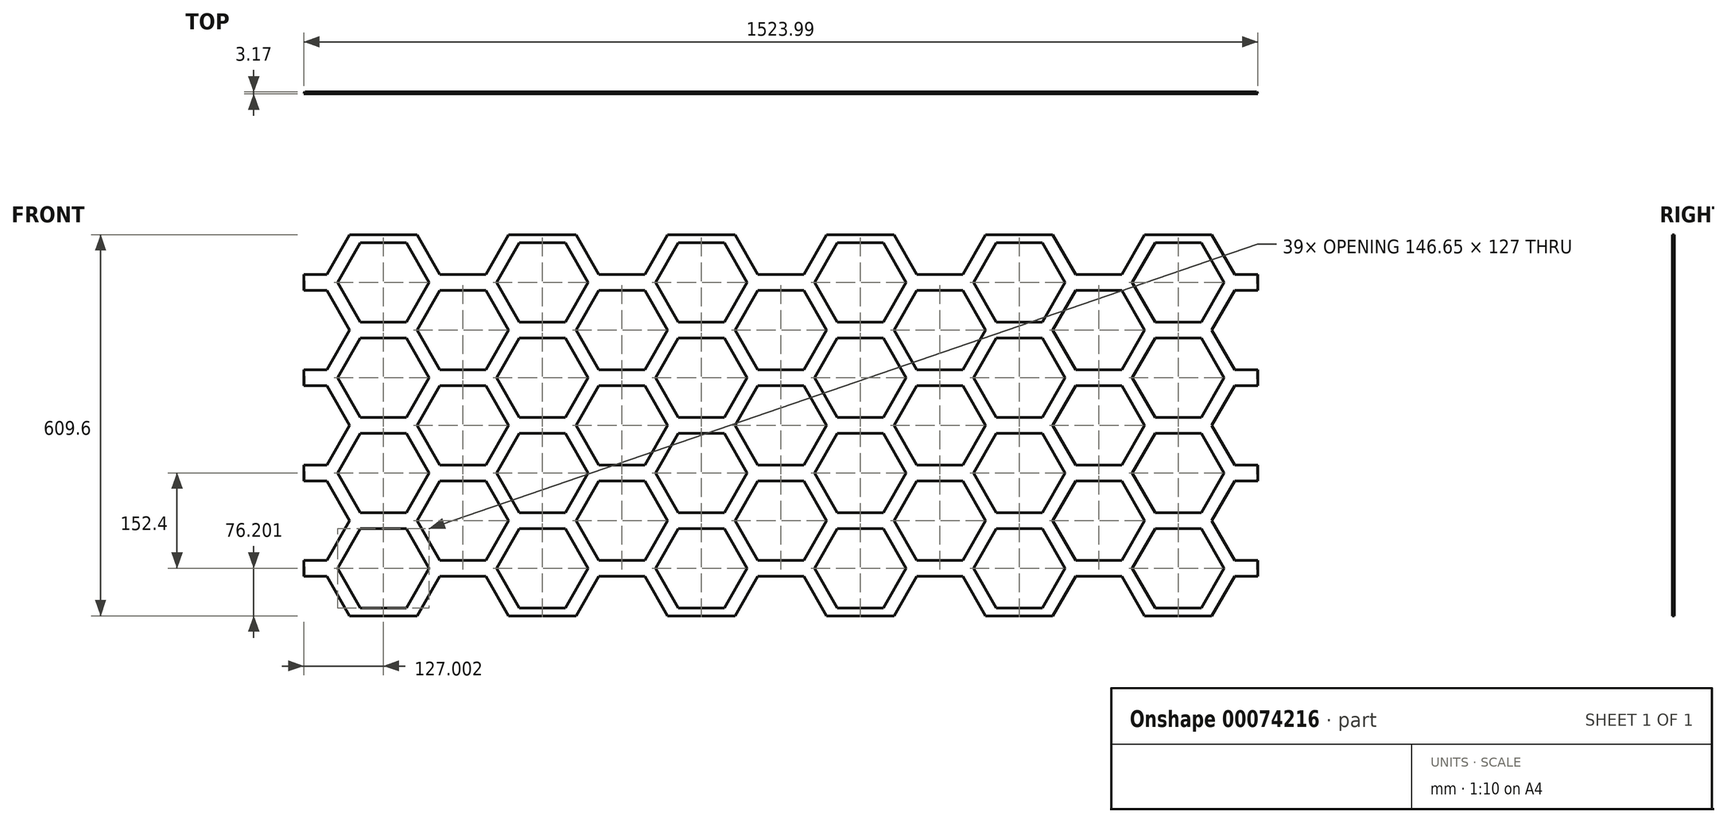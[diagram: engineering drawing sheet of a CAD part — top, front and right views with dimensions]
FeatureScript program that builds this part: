
annotation { "Feature Type Name" : "Feature", "Feature Type Description" : "" }
export const myFeature = defineFeature(function(context is Context, id is Id, definition is map)
    precondition{}
    {
        {
            var Q0;
            Q0=qCreatedBy(makeId("Front.planeOp"),FACE);
            var sketch = newSketch(context, id + "F0", { "sketchPlane" : qUnion([Q0])});
            skLineSegment(sketch, "E0.bottom", {"start": v(-531.26, 319.5) * mm, "end": v(992.74, 319.5) * mm});
            skLineSegment(sketch, "E0.top", {"start": v(-531.26, -290.1) * mm, "end": v(992.74, -290.1) * mm});
            skLineSegment(sketch, "E0.left", {"start": v(-531.26, 319.5) * mm, "end": v(-531.26, -290.1) * mm});
            skLineSegment(sketch, "E0.right", {"start": v(992.74, 319.5) * mm, "end": v(992.74, -290.1) * mm});
            skCircle(sketch, "E1.cCircle", {"center": v(-531.26, -290.1) * mm, "radius": 63.5 * mm, "construction": true});
            skLineSegment(sketch, "E1.0", {"start": v(-567.92, -226.6) * mm, "end": v(-494.6, -226.6) * mm});
            skLineSegment(sketch, "E1.1", {"start": v(-494.6, -226.6) * mm, "end": v(-457.93, -290.1) * mm});
            skLineSegment(sketch, "E1.2", {"start": v(-457.93, -290.1) * mm, "end": v(-494.6, -353.6) * mm});
            skLineSegment(sketch, "E1.3", {"start": v(-494.6, -353.6) * mm, "end": v(-567.92, -353.6) * mm});
            skLineSegment(sketch, "E1.4", {"start": v(-567.92, -353.6) * mm, "end": v(-604.58, -290.1) * mm});
            skLineSegment(sketch, "E1.5", {"start": v(-604.58, -290.1) * mm, "end": v(-567.92, -226.6) * mm});
            skPoint(sketch, "E1.0.midPoint", {"position": v(-531.26, -226.6) * mm});
            skLineSegment(sketch, "E2", {"start": v(-531.26, -290.1) * mm, "end": v(-404.26, -290.1) * mm, "construction": true});
            skLineSegment(sketch, "E3", {"start": v(-404.26, -290.1) * mm, "end": v(-404.26, -213.9) * mm, "construction": true});
            skCircle(sketch, "E4.cCircle", {"center": v(-404.26, -213.9) * mm, "radius": 63.5 * mm, "construction": true});
            skLineSegment(sketch, "E4.0", {"start": v(-440.92, -150.4) * mm, "end": v(-367.6, -150.4) * mm});
            skLineSegment(sketch, "E4.1", {"start": v(-367.6, -150.4) * mm, "end": v(-330.93, -213.9) * mm});
            skLineSegment(sketch, "E4.2", {"start": v(-330.93, -213.9) * mm, "end": v(-367.6, -277.4) * mm});
            skLineSegment(sketch, "E4.3", {"start": v(-367.6, -277.4) * mm, "end": v(-440.92, -277.4) * mm});
            skLineSegment(sketch, "E4.4", {"start": v(-440.92, -277.4) * mm, "end": v(-477.58, -213.9) * mm});
            skLineSegment(sketch, "E4.5", {"start": v(-477.58, -213.9) * mm, "end": v(-440.92, -150.4) * mm});
            skPoint(sketch, "E4.0.midPoint", {"position": v(-404.26, -150.4) * mm});
            skLineSegment(sketch, "E5.0.1.0", {"start": v(-457.93, -137.7) * mm, "end": v(-494.6, -201.2) * mm});
            skLineSegment(sketch, "E5.0.1.1", {"start": v(-494.6, -201.2) * mm, "end": v(-567.92, -201.2) * mm});
            skLineSegment(sketch, "E5.0.1.2", {"start": v(-567.92, -74.2) * mm, "end": v(-494.6, -74.2) * mm});
            skLineSegment(sketch, "E5.0.1.3", {"start": v(-567.92, -201.2) * mm, "end": v(-604.58, -137.7) * mm});
            skLineSegment(sketch, "E5.0.1.4", {"start": v(-494.6, -74.2) * mm, "end": v(-457.93, -137.7) * mm});
            skLineSegment(sketch, "E5.0.1.5", {"start": v(-604.58, -137.7) * mm, "end": v(-567.92, -74.2) * mm});
            skLineSegment(sketch, "E5.0.2.0", {"start": v(-457.93, 14.7) * mm, "end": v(-494.6, -48.8) * mm});
            skLineSegment(sketch, "E5.0.2.1", {"start": v(-494.6, -48.8) * mm, "end": v(-567.92, -48.8) * mm});
            skLineSegment(sketch, "E5.0.2.2", {"start": v(-567.92, 78.2) * mm, "end": v(-494.6, 78.2) * mm});
            skLineSegment(sketch, "E5.0.2.3", {"start": v(-567.92, -48.8) * mm, "end": v(-604.58, 14.7) * mm});
            skLineSegment(sketch, "E5.0.2.4", {"start": v(-494.6, 78.2) * mm, "end": v(-457.93, 14.7) * mm});
            skLineSegment(sketch, "E5.0.2.5", {"start": v(-604.58, 14.7) * mm, "end": v(-567.92, 78.2) * mm});
            skLineSegment(sketch, "E5.0.3.0", {"start": v(-457.93, 167.1) * mm, "end": v(-494.6, 103.6) * mm});
            skLineSegment(sketch, "E5.0.3.1", {"start": v(-494.6, 103.6) * mm, "end": v(-567.92, 103.6) * mm});
            skLineSegment(sketch, "E5.0.3.2", {"start": v(-567.92, 230.6) * mm, "end": v(-494.6, 230.6) * mm});
            skLineSegment(sketch, "E5.0.3.3", {"start": v(-567.92, 103.6) * mm, "end": v(-604.58, 167.1) * mm});
            skLineSegment(sketch, "E5.0.3.4", {"start": v(-494.6, 230.6) * mm, "end": v(-457.93, 167.1) * mm});
            skLineSegment(sketch, "E5.0.3.5", {"start": v(-604.58, 167.1) * mm, "end": v(-567.92, 230.6) * mm});
            skLineSegment(sketch, "E5.0.4.0", {"start": v(-457.93, 319.5) * mm, "end": v(-494.6, 256) * mm});
            skLineSegment(sketch, "E5.0.4.1", {"start": v(-494.6, 256) * mm, "end": v(-567.92, 256) * mm});
            skLineSegment(sketch, "E5.0.4.2", {"start": v(-567.92, 383) * mm, "end": v(-494.6, 383) * mm});
            skLineSegment(sketch, "E5.0.4.3", {"start": v(-567.92, 256) * mm, "end": v(-604.58, 319.5) * mm});
            skLineSegment(sketch, "E5.0.4.4", {"start": v(-494.6, 383) * mm, "end": v(-457.93, 319.5) * mm});
            skLineSegment(sketch, "E5.0.4.5", {"start": v(-604.58, 319.5) * mm, "end": v(-567.92, 383) * mm});
            skLineSegment(sketch, "E5.1.0.0", {"start": v(-203.93, -290.1) * mm, "end": v(-240.6, -353.6) * mm});
            skLineSegment(sketch, "E5.1.0.1", {"start": v(-240.6, -353.6) * mm, "end": v(-313.92, -353.6) * mm});
            skLineSegment(sketch, "E5.1.0.2", {"start": v(-313.92, -226.6) * mm, "end": v(-240.6, -226.6) * mm});
            skLineSegment(sketch, "E5.1.0.3", {"start": v(-313.92, -353.6) * mm, "end": v(-350.58, -290.1) * mm});
            skLineSegment(sketch, "E5.1.0.4", {"start": v(-240.6, -226.6) * mm, "end": v(-203.93, -290.1) * mm});
            skLineSegment(sketch, "E5.1.0.5", {"start": v(-350.58, -290.1) * mm, "end": v(-313.92, -226.6) * mm});
            skLineSegment(sketch, "E5.1.1.0", {"start": v(-203.93, -137.7) * mm, "end": v(-240.6, -201.2) * mm});
            skLineSegment(sketch, "E5.1.1.1", {"start": v(-240.6, -201.2) * mm, "end": v(-313.92, -201.2) * mm});
            skLineSegment(sketch, "E5.1.1.2", {"start": v(-313.92, -74.2) * mm, "end": v(-240.6, -74.2) * mm});
            skLineSegment(sketch, "E5.1.1.3", {"start": v(-313.92, -201.2) * mm, "end": v(-350.58, -137.7) * mm});
            skLineSegment(sketch, "E5.1.1.4", {"start": v(-240.6, -74.2) * mm, "end": v(-203.93, -137.7) * mm});
            skLineSegment(sketch, "E5.1.1.5", {"start": v(-350.58, -137.7) * mm, "end": v(-313.92, -74.2) * mm});
            skLineSegment(sketch, "E5.1.2.0", {"start": v(-203.93, 14.7) * mm, "end": v(-240.6, -48.8) * mm});
            skLineSegment(sketch, "E5.1.2.1", {"start": v(-240.6, -48.8) * mm, "end": v(-313.92, -48.8) * mm});
            skLineSegment(sketch, "E5.1.2.2", {"start": v(-313.92, 78.2) * mm, "end": v(-240.6, 78.2) * mm});
            skLineSegment(sketch, "E5.1.2.3", {"start": v(-313.92, -48.8) * mm, "end": v(-350.58, 14.7) * mm});
            skLineSegment(sketch, "E5.1.2.4", {"start": v(-240.6, 78.2) * mm, "end": v(-203.93, 14.7) * mm});
            skLineSegment(sketch, "E5.1.2.5", {"start": v(-350.58, 14.7) * mm, "end": v(-313.92, 78.2) * mm});
            skLineSegment(sketch, "E5.1.3.0", {"start": v(-203.93, 167.1) * mm, "end": v(-240.6, 103.6) * mm});
            skLineSegment(sketch, "E5.1.3.1", {"start": v(-240.6, 103.6) * mm, "end": v(-313.92, 103.6) * mm});
            skLineSegment(sketch, "E5.1.3.2", {"start": v(-313.92, 230.6) * mm, "end": v(-240.6, 230.6) * mm});
            skLineSegment(sketch, "E5.1.3.3", {"start": v(-313.92, 103.6) * mm, "end": v(-350.58, 167.1) * mm});
            skLineSegment(sketch, "E5.1.3.4", {"start": v(-240.6, 230.6) * mm, "end": v(-203.93, 167.1) * mm});
            skLineSegment(sketch, "E5.1.3.5", {"start": v(-350.58, 167.1) * mm, "end": v(-313.92, 230.6) * mm});
            skLineSegment(sketch, "E5.1.4.0", {"start": v(-203.93, 319.5) * mm, "end": v(-240.6, 256) * mm});
            skLineSegment(sketch, "E5.1.4.1", {"start": v(-240.6, 256) * mm, "end": v(-313.92, 256) * mm});
            skLineSegment(sketch, "E5.1.4.2", {"start": v(-313.92, 383) * mm, "end": v(-240.6, 383) * mm});
            skLineSegment(sketch, "E5.1.4.3", {"start": v(-313.92, 256) * mm, "end": v(-350.58, 319.5) * mm});
            skLineSegment(sketch, "E5.1.4.4", {"start": v(-240.6, 383) * mm, "end": v(-203.93, 319.5) * mm});
            skLineSegment(sketch, "E5.1.4.5", {"start": v(-350.58, 319.5) * mm, "end": v(-313.92, 383) * mm});
            skLineSegment(sketch, "E5.2.0.0", {"start": v(50.07, -290.1) * mm, "end": v(13.4, -353.6) * mm});
            skLineSegment(sketch, "E5.2.0.1", {"start": v(13.4, -353.6) * mm, "end": v(-59.92, -353.6) * mm});
            skLineSegment(sketch, "E5.2.0.2", {"start": v(-59.92, -226.6) * mm, "end": v(13.4, -226.6) * mm});
            skLineSegment(sketch, "E5.2.0.3", {"start": v(-59.92, -353.6) * mm, "end": v(-96.58, -290.1) * mm});
            skLineSegment(sketch, "E5.2.0.4", {"start": v(13.4, -226.6) * mm, "end": v(50.07, -290.1) * mm});
            skLineSegment(sketch, "E5.2.0.5", {"start": v(-96.58, -290.1) * mm, "end": v(-59.92, -226.6) * mm});
            skLineSegment(sketch, "E5.2.1.0", {"start": v(50.07, -137.7) * mm, "end": v(13.4, -201.2) * mm});
            skLineSegment(sketch, "E5.2.1.1", {"start": v(13.4, -201.2) * mm, "end": v(-59.92, -201.2) * mm});
            skLineSegment(sketch, "E5.2.1.2", {"start": v(-59.92, -74.2) * mm, "end": v(13.4, -74.2) * mm});
            skLineSegment(sketch, "E5.2.1.3", {"start": v(-59.92, -201.2) * mm, "end": v(-96.58, -137.7) * mm});
            skLineSegment(sketch, "E5.2.1.4", {"start": v(13.4, -74.2) * mm, "end": v(50.07, -137.7) * mm});
            skLineSegment(sketch, "E5.2.1.5", {"start": v(-96.58, -137.7) * mm, "end": v(-59.92, -74.2) * mm});
            skLineSegment(sketch, "E5.2.2.0", {"start": v(50.07, 14.7) * mm, "end": v(13.4, -48.8) * mm});
            skLineSegment(sketch, "E5.2.2.1", {"start": v(13.4, -48.8) * mm, "end": v(-59.92, -48.8) * mm});
            skLineSegment(sketch, "E5.2.2.2", {"start": v(-59.92, 78.2) * mm, "end": v(13.4, 78.2) * mm});
            skLineSegment(sketch, "E5.2.2.3", {"start": v(-59.92, -48.8) * mm, "end": v(-96.58, 14.7) * mm});
            skLineSegment(sketch, "E5.2.2.4", {"start": v(13.4, 78.2) * mm, "end": v(50.07, 14.7) * mm});
            skLineSegment(sketch, "E5.2.2.5", {"start": v(-96.58, 14.7) * mm, "end": v(-59.92, 78.2) * mm});
            skLineSegment(sketch, "E5.2.3.0", {"start": v(50.07, 167.1) * mm, "end": v(13.4, 103.6) * mm});
            skLineSegment(sketch, "E5.2.3.1", {"start": v(13.4, 103.6) * mm, "end": v(-59.92, 103.6) * mm});
            skLineSegment(sketch, "E5.2.3.2", {"start": v(-59.92, 230.6) * mm, "end": v(13.4, 230.6) * mm});
            skLineSegment(sketch, "E5.2.3.3", {"start": v(-59.92, 103.6) * mm, "end": v(-96.58, 167.1) * mm});
            skLineSegment(sketch, "E5.2.3.4", {"start": v(13.4, 230.6) * mm, "end": v(50.07, 167.1) * mm});
            skLineSegment(sketch, "E5.2.3.5", {"start": v(-96.58, 167.1) * mm, "end": v(-59.92, 230.6) * mm});
            skLineSegment(sketch, "E5.2.4.0", {"start": v(50.07, 319.5) * mm, "end": v(13.4, 256) * mm});
            skLineSegment(sketch, "E5.2.4.1", {"start": v(13.4, 256) * mm, "end": v(-59.92, 256) * mm});
            skLineSegment(sketch, "E5.2.4.2", {"start": v(-59.92, 383) * mm, "end": v(13.4, 383) * mm});
            skLineSegment(sketch, "E5.2.4.3", {"start": v(-59.92, 256) * mm, "end": v(-96.58, 319.5) * mm});
            skLineSegment(sketch, "E5.2.4.4", {"start": v(13.4, 383) * mm, "end": v(50.07, 319.5) * mm});
            skLineSegment(sketch, "E5.2.4.5", {"start": v(-96.58, 319.5) * mm, "end": v(-59.92, 383) * mm});
            skLineSegment(sketch, "E5.3.0.0", {"start": v(304.07, -290.1) * mm, "end": v(267.4, -353.6) * mm});
            skLineSegment(sketch, "E5.3.0.1", {"start": v(267.4, -353.6) * mm, "end": v(194.08, -353.6) * mm});
            skLineSegment(sketch, "E5.3.0.2", {"start": v(194.08, -226.6) * mm, "end": v(267.4, -226.6) * mm});
            skLineSegment(sketch, "E5.3.0.3", {"start": v(194.08, -353.6) * mm, "end": v(157.42, -290.1) * mm});
            skLineSegment(sketch, "E5.3.0.4", {"start": v(267.4, -226.6) * mm, "end": v(304.07, -290.1) * mm});
            skLineSegment(sketch, "E5.3.0.5", {"start": v(157.42, -290.1) * mm, "end": v(194.08, -226.6) * mm});
            skLineSegment(sketch, "E5.3.1.0", {"start": v(304.07, -137.7) * mm, "end": v(267.4, -201.2) * mm});
            skLineSegment(sketch, "E5.3.1.1", {"start": v(267.4, -201.2) * mm, "end": v(194.08, -201.2) * mm});
            skLineSegment(sketch, "E5.3.1.2", {"start": v(194.08, -74.2) * mm, "end": v(267.4, -74.2) * mm});
            skLineSegment(sketch, "E5.3.1.3", {"start": v(194.08, -201.2) * mm, "end": v(157.42, -137.7) * mm});
            skLineSegment(sketch, "E5.3.1.4", {"start": v(267.4, -74.2) * mm, "end": v(304.07, -137.7) * mm});
            skLineSegment(sketch, "E5.3.1.5", {"start": v(157.42, -137.7) * mm, "end": v(194.08, -74.2) * mm});
            skLineSegment(sketch, "E5.3.2.0", {"start": v(304.07, 14.7) * mm, "end": v(267.4, -48.8) * mm});
            skLineSegment(sketch, "E5.3.2.1", {"start": v(267.4, -48.8) * mm, "end": v(194.08, -48.8) * mm});
            skLineSegment(sketch, "E5.3.2.2", {"start": v(194.08, 78.2) * mm, "end": v(267.4, 78.2) * mm});
            skLineSegment(sketch, "E5.3.2.3", {"start": v(194.08, -48.8) * mm, "end": v(157.42, 14.7) * mm});
            skLineSegment(sketch, "E5.3.2.4", {"start": v(267.4, 78.2) * mm, "end": v(304.07, 14.7) * mm});
            skLineSegment(sketch, "E5.3.2.5", {"start": v(157.42, 14.7) * mm, "end": v(194.08, 78.2) * mm});
            skLineSegment(sketch, "E5.3.3.0", {"start": v(304.07, 167.1) * mm, "end": v(267.4, 103.6) * mm});
            skLineSegment(sketch, "E5.3.3.1", {"start": v(267.4, 103.6) * mm, "end": v(194.08, 103.6) * mm});
            skLineSegment(sketch, "E5.3.3.2", {"start": v(194.08, 230.6) * mm, "end": v(267.4, 230.6) * mm});
            skLineSegment(sketch, "E5.3.3.3", {"start": v(194.08, 103.6) * mm, "end": v(157.42, 167.1) * mm});
            skLineSegment(sketch, "E5.3.3.4", {"start": v(267.4, 230.6) * mm, "end": v(304.07, 167.1) * mm});
            skLineSegment(sketch, "E5.3.3.5", {"start": v(157.42, 167.1) * mm, "end": v(194.08, 230.6) * mm});
            skLineSegment(sketch, "E5.3.4.0", {"start": v(304.07, 319.5) * mm, "end": v(267.4, 256) * mm});
            skLineSegment(sketch, "E5.3.4.1", {"start": v(267.4, 256) * mm, "end": v(194.08, 256) * mm});
            skLineSegment(sketch, "E5.3.4.2", {"start": v(194.08, 383) * mm, "end": v(267.4, 383) * mm});
            skLineSegment(sketch, "E5.3.4.3", {"start": v(194.08, 256) * mm, "end": v(157.42, 319.5) * mm});
            skLineSegment(sketch, "E5.3.4.4", {"start": v(267.4, 383) * mm, "end": v(304.07, 319.5) * mm});
            skLineSegment(sketch, "E5.3.4.5", {"start": v(157.42, 319.5) * mm, "end": v(194.08, 383) * mm});
            skLineSegment(sketch, "E5.4.0.0", {"start": v(558.07, -290.1) * mm, "end": v(521.4, -353.6) * mm});
            skLineSegment(sketch, "E5.4.0.1", {"start": v(521.4, -353.6) * mm, "end": v(448.08, -353.6) * mm});
            skLineSegment(sketch, "E5.4.0.2", {"start": v(448.08, -226.6) * mm, "end": v(521.4, -226.6) * mm});
            skLineSegment(sketch, "E5.4.0.3", {"start": v(448.08, -353.6) * mm, "end": v(411.42, -290.1) * mm});
            skLineSegment(sketch, "E5.4.0.4", {"start": v(521.4, -226.6) * mm, "end": v(558.07, -290.1) * mm});
            skLineSegment(sketch, "E5.4.0.5", {"start": v(411.42, -290.1) * mm, "end": v(448.08, -226.6) * mm});
            skLineSegment(sketch, "E5.4.1.0", {"start": v(558.07, -137.7) * mm, "end": v(521.4, -201.2) * mm});
            skLineSegment(sketch, "E5.4.1.1", {"start": v(521.4, -201.2) * mm, "end": v(448.08, -201.2) * mm});
            skLineSegment(sketch, "E5.4.1.2", {"start": v(448.08, -74.2) * mm, "end": v(521.4, -74.2) * mm});
            skLineSegment(sketch, "E5.4.1.3", {"start": v(448.08, -201.2) * mm, "end": v(411.42, -137.7) * mm});
            skLineSegment(sketch, "E5.4.1.4", {"start": v(521.4, -74.2) * mm, "end": v(558.07, -137.7) * mm});
            skLineSegment(sketch, "E5.4.1.5", {"start": v(411.42, -137.7) * mm, "end": v(448.08, -74.2) * mm});
            skLineSegment(sketch, "E5.4.2.0", {"start": v(558.07, 14.7) * mm, "end": v(521.4, -48.8) * mm});
            skLineSegment(sketch, "E5.4.2.1", {"start": v(521.4, -48.8) * mm, "end": v(448.08, -48.8) * mm});
            skLineSegment(sketch, "E5.4.2.2", {"start": v(448.08, 78.2) * mm, "end": v(521.4, 78.2) * mm});
            skLineSegment(sketch, "E5.4.2.3", {"start": v(448.08, -48.8) * mm, "end": v(411.42, 14.7) * mm});
            skLineSegment(sketch, "E5.4.2.4", {"start": v(521.4, 78.2) * mm, "end": v(558.07, 14.7) * mm});
            skLineSegment(sketch, "E5.4.2.5", {"start": v(411.42, 14.7) * mm, "end": v(448.08, 78.2) * mm});
            skLineSegment(sketch, "E5.4.3.0", {"start": v(558.07, 167.1) * mm, "end": v(521.4, 103.6) * mm});
            skLineSegment(sketch, "E5.4.3.1", {"start": v(521.4, 103.6) * mm, "end": v(448.08, 103.6) * mm});
            skLineSegment(sketch, "E5.4.3.2", {"start": v(448.08, 230.6) * mm, "end": v(521.4, 230.6) * mm});
            skLineSegment(sketch, "E5.4.3.3", {"start": v(448.08, 103.6) * mm, "end": v(411.42, 167.1) * mm});
            skLineSegment(sketch, "E5.4.3.4", {"start": v(521.4, 230.6) * mm, "end": v(558.07, 167.1) * mm});
            skLineSegment(sketch, "E5.4.3.5", {"start": v(411.42, 167.1) * mm, "end": v(448.08, 230.6) * mm});
            skLineSegment(sketch, "E5.4.4.0", {"start": v(558.07, 319.5) * mm, "end": v(521.4, 256) * mm});
            skLineSegment(sketch, "E5.4.4.1", {"start": v(521.4, 256) * mm, "end": v(448.08, 256) * mm});
            skLineSegment(sketch, "E5.4.4.2", {"start": v(448.08, 383) * mm, "end": v(521.4, 383) * mm});
            skLineSegment(sketch, "E5.4.4.3", {"start": v(448.08, 256) * mm, "end": v(411.42, 319.5) * mm});
            skLineSegment(sketch, "E5.4.4.4", {"start": v(521.4, 383) * mm, "end": v(558.07, 319.5) * mm});
            skLineSegment(sketch, "E5.4.4.5", {"start": v(411.42, 319.5) * mm, "end": v(448.08, 383) * mm});
            skLineSegment(sketch, "E5.5.0.0", {"start": v(812.07, -290.1) * mm, "end": v(775.4, -353.6) * mm});
            skLineSegment(sketch, "E5.5.0.1", {"start": v(775.4, -353.6) * mm, "end": v(702.08, -353.6) * mm});
            skLineSegment(sketch, "E5.5.0.2", {"start": v(702.08, -226.6) * mm, "end": v(775.4, -226.6) * mm});
            skLineSegment(sketch, "E5.5.0.3", {"start": v(702.08, -353.6) * mm, "end": v(665.42, -290.1) * mm});
            skLineSegment(sketch, "E5.5.0.4", {"start": v(775.4, -226.6) * mm, "end": v(812.07, -290.1) * mm});
            skLineSegment(sketch, "E5.5.0.5", {"start": v(665.42, -290.1) * mm, "end": v(702.08, -226.6) * mm});
            skLineSegment(sketch, "E5.5.1.0", {"start": v(812.07, -137.7) * mm, "end": v(775.4, -201.2) * mm});
            skLineSegment(sketch, "E5.5.1.1", {"start": v(775.4, -201.2) * mm, "end": v(702.08, -201.2) * mm});
            skLineSegment(sketch, "E5.5.1.2", {"start": v(702.08, -74.2) * mm, "end": v(775.4, -74.2) * mm});
            skLineSegment(sketch, "E5.5.1.3", {"start": v(702.08, -201.2) * mm, "end": v(665.42, -137.7) * mm});
            skLineSegment(sketch, "E5.5.1.4", {"start": v(775.4, -74.2) * mm, "end": v(812.07, -137.7) * mm});
            skLineSegment(sketch, "E5.5.1.5", {"start": v(665.42, -137.7) * mm, "end": v(702.08, -74.2) * mm});
            skLineSegment(sketch, "E5.5.2.0", {"start": v(812.07, 14.7) * mm, "end": v(775.4, -48.8) * mm});
            skLineSegment(sketch, "E5.5.2.1", {"start": v(775.4, -48.8) * mm, "end": v(702.08, -48.8) * mm});
            skLineSegment(sketch, "E5.5.2.2", {"start": v(702.08, 78.2) * mm, "end": v(775.4, 78.2) * mm});
            skLineSegment(sketch, "E5.5.2.3", {"start": v(702.08, -48.8) * mm, "end": v(665.42, 14.7) * mm});
            skLineSegment(sketch, "E5.5.2.4", {"start": v(775.4, 78.2) * mm, "end": v(812.07, 14.7) * mm});
            skLineSegment(sketch, "E5.5.2.5", {"start": v(665.42, 14.7) * mm, "end": v(702.08, 78.2) * mm});
            skLineSegment(sketch, "E5.5.3.0", {"start": v(812.07, 167.1) * mm, "end": v(775.4, 103.6) * mm});
            skLineSegment(sketch, "E5.5.3.1", {"start": v(775.4, 103.6) * mm, "end": v(702.08, 103.6) * mm});
            skLineSegment(sketch, "E5.5.3.2", {"start": v(702.08, 230.6) * mm, "end": v(775.4, 230.6) * mm});
            skLineSegment(sketch, "E5.5.3.3", {"start": v(702.08, 103.6) * mm, "end": v(665.42, 167.1) * mm});
            skLineSegment(sketch, "E5.5.3.4", {"start": v(775.4, 230.6) * mm, "end": v(812.07, 167.1) * mm});
            skLineSegment(sketch, "E5.5.3.5", {"start": v(665.42, 167.1) * mm, "end": v(702.08, 230.6) * mm});
            skLineSegment(sketch, "E5.5.4.0", {"start": v(812.07, 319.5) * mm, "end": v(775.4, 256) * mm});
            skLineSegment(sketch, "E5.5.4.1", {"start": v(775.4, 256) * mm, "end": v(702.08, 256) * mm});
            skLineSegment(sketch, "E5.5.4.2", {"start": v(702.08, 383) * mm, "end": v(775.4, 383) * mm});
            skLineSegment(sketch, "E5.5.4.3", {"start": v(702.08, 256) * mm, "end": v(665.42, 319.5) * mm});
            skLineSegment(sketch, "E5.5.4.4", {"start": v(775.4, 383) * mm, "end": v(812.07, 319.5) * mm});
            skLineSegment(sketch, "E5.5.4.5", {"start": v(665.42, 319.5) * mm, "end": v(702.08, 383) * mm});
            skLineSegment(sketch, "E5.6.0.0", {"start": v(1066.07, -290.1) * mm, "end": v(1029.4, -353.6) * mm});
            skLineSegment(sketch, "E5.6.0.1", {"start": v(1029.4, -353.6) * mm, "end": v(956.08, -353.6) * mm});
            skLineSegment(sketch, "E5.6.0.2", {"start": v(956.08, -226.6) * mm, "end": v(1029.4, -226.6) * mm});
            skLineSegment(sketch, "E5.6.0.3", {"start": v(956.08, -353.6) * mm, "end": v(919.42, -290.1) * mm});
            skLineSegment(sketch, "E5.6.0.4", {"start": v(1029.4, -226.6) * mm, "end": v(1066.07, -290.1) * mm});
            skLineSegment(sketch, "E5.6.0.5", {"start": v(919.42, -290.1) * mm, "end": v(956.08, -226.6) * mm});
            skLineSegment(sketch, "E5.6.1.0", {"start": v(1066.07, -137.7) * mm, "end": v(1029.4, -201.2) * mm});
            skLineSegment(sketch, "E5.6.1.1", {"start": v(1029.4, -201.2) * mm, "end": v(956.08, -201.2) * mm});
            skLineSegment(sketch, "E5.6.1.2", {"start": v(956.08, -74.2) * mm, "end": v(1029.4, -74.2) * mm});
            skLineSegment(sketch, "E5.6.1.3", {"start": v(956.08, -201.2) * mm, "end": v(919.42, -137.7) * mm});
            skLineSegment(sketch, "E5.6.1.4", {"start": v(1029.4, -74.2) * mm, "end": v(1066.07, -137.7) * mm});
            skLineSegment(sketch, "E5.6.1.5", {"start": v(919.42, -137.7) * mm, "end": v(956.08, -74.2) * mm});
            skLineSegment(sketch, "E5.6.2.0", {"start": v(1066.07, 14.7) * mm, "end": v(1029.4, -48.8) * mm});
            skLineSegment(sketch, "E5.6.2.1", {"start": v(1029.4, -48.8) * mm, "end": v(956.08, -48.8) * mm});
            skLineSegment(sketch, "E5.6.2.2", {"start": v(956.08, 78.2) * mm, "end": v(1029.4, 78.2) * mm});
            skLineSegment(sketch, "E5.6.2.3", {"start": v(956.08, -48.8) * mm, "end": v(919.42, 14.7) * mm});
            skLineSegment(sketch, "E5.6.2.4", {"start": v(1029.4, 78.2) * mm, "end": v(1066.07, 14.7) * mm});
            skLineSegment(sketch, "E5.6.2.5", {"start": v(919.42, 14.7) * mm, "end": v(956.08, 78.2) * mm});
            skLineSegment(sketch, "E5.6.3.0", {"start": v(1066.07, 167.1) * mm, "end": v(1029.4, 103.6) * mm});
            skLineSegment(sketch, "E5.6.3.1", {"start": v(1029.4, 103.6) * mm, "end": v(956.08, 103.6) * mm});
            skLineSegment(sketch, "E5.6.3.2", {"start": v(956.08, 230.6) * mm, "end": v(1029.4, 230.6) * mm});
            skLineSegment(sketch, "E5.6.3.3", {"start": v(956.08, 103.6) * mm, "end": v(919.42, 167.1) * mm});
            skLineSegment(sketch, "E5.6.3.4", {"start": v(1029.4, 230.6) * mm, "end": v(1066.07, 167.1) * mm});
            skLineSegment(sketch, "E5.6.3.5", {"start": v(919.42, 167.1) * mm, "end": v(956.08, 230.6) * mm});
            skLineSegment(sketch, "E5.6.4.0", {"start": v(1066.07, 319.5) * mm, "end": v(1029.4, 256) * mm});
            skLineSegment(sketch, "E5.6.4.1", {"start": v(1029.4, 256) * mm, "end": v(956.08, 256) * mm});
            skLineSegment(sketch, "E5.6.4.2", {"start": v(956.08, 383) * mm, "end": v(1029.4, 383) * mm});
            skLineSegment(sketch, "E5.6.4.3", {"start": v(956.08, 256) * mm, "end": v(919.42, 319.5) * mm});
            skLineSegment(sketch, "E5.6.4.4", {"start": v(1029.4, 383) * mm, "end": v(1066.07, 319.5) * mm});
            skLineSegment(sketch, "E5.6.4.5", {"start": v(919.42, 319.5) * mm, "end": v(956.08, 383) * mm});
            skLineSegment(sketch, "E5.direction1", {"start": v(-604.58, -290.1) * mm, "end": v(-350.58, -290.1) * mm, "construction": true});
            skLineSegment(sketch, "E5.direction2", {"start": v(-604.58, -290.1) * mm, "end": v(-604.58, -137.7) * mm, "construction": true});
            skLineSegment(sketch, "E6.0.1.0", {"start": v(-440.92, -125) * mm, "end": v(-477.58, -61.5) * mm});
            skLineSegment(sketch, "E6.0.1.1", {"start": v(-367.6, 2) * mm, "end": v(-330.93, -61.5) * mm});
            skLineSegment(sketch, "E6.0.1.2", {"start": v(-477.58, -61.5) * mm, "end": v(-440.92, 2) * mm});
            skLineSegment(sketch, "E6.0.1.3", {"start": v(-330.93, -61.5) * mm, "end": v(-367.6, -125) * mm});
            skLineSegment(sketch, "E6.0.1.4", {"start": v(-367.6, -125) * mm, "end": v(-440.92, -125) * mm});
            skLineSegment(sketch, "E6.0.1.5", {"start": v(-440.92, 2) * mm, "end": v(-367.6, 2) * mm});
            skLineSegment(sketch, "E6.0.2.0", {"start": v(-440.92, 27.4) * mm, "end": v(-477.58, 90.9) * mm});
            skLineSegment(sketch, "E6.0.2.1", {"start": v(-367.6, 154.4) * mm, "end": v(-330.93, 90.9) * mm});
            skLineSegment(sketch, "E6.0.2.2", {"start": v(-477.58, 90.9) * mm, "end": v(-440.92, 154.4) * mm});
            skLineSegment(sketch, "E6.0.2.3", {"start": v(-330.93, 90.9) * mm, "end": v(-367.6, 27.4) * mm});
            skLineSegment(sketch, "E6.0.2.4", {"start": v(-367.6, 27.4) * mm, "end": v(-440.92, 27.4) * mm});
            skLineSegment(sketch, "E6.0.2.5", {"start": v(-440.92, 154.4) * mm, "end": v(-367.6, 154.4) * mm});
            skLineSegment(sketch, "E6.0.3.0", {"start": v(-440.92, 179.8) * mm, "end": v(-477.58, 243.3) * mm});
            skLineSegment(sketch, "E6.0.3.1", {"start": v(-367.6, 306.8) * mm, "end": v(-330.93, 243.3) * mm});
            skLineSegment(sketch, "E6.0.3.2", {"start": v(-477.58, 243.3) * mm, "end": v(-440.92, 306.8) * mm});
            skLineSegment(sketch, "E6.0.3.3", {"start": v(-330.93, 243.3) * mm, "end": v(-367.6, 179.8) * mm});
            skLineSegment(sketch, "E6.0.3.4", {"start": v(-367.6, 179.8) * mm, "end": v(-440.92, 179.8) * mm});
            skLineSegment(sketch, "E6.0.3.5", {"start": v(-440.92, 306.8) * mm, "end": v(-367.6, 306.8) * mm});
            skLineSegment(sketch, "E6.1.0.0", {"start": v(-186.92, -277.4) * mm, "end": v(-223.58, -213.9) * mm});
            skLineSegment(sketch, "E6.1.0.1", {"start": v(-113.6, -150.4) * mm, "end": v(-76.93, -213.9) * mm});
            skLineSegment(sketch, "E6.1.0.2", {"start": v(-223.58, -213.9) * mm, "end": v(-186.92, -150.4) * mm});
            skLineSegment(sketch, "E6.1.0.3", {"start": v(-76.93, -213.9) * mm, "end": v(-113.6, -277.4) * mm});
            skLineSegment(sketch, "E6.1.0.4", {"start": v(-113.6, -277.4) * mm, "end": v(-186.92, -277.4) * mm});
            skLineSegment(sketch, "E6.1.0.5", {"start": v(-186.92, -150.4) * mm, "end": v(-113.6, -150.4) * mm});
            skLineSegment(sketch, "E6.1.1.0", {"start": v(-186.92, -125) * mm, "end": v(-223.58, -61.5) * mm});
            skLineSegment(sketch, "E6.1.1.1", {"start": v(-113.6, 2) * mm, "end": v(-76.93, -61.5) * mm});
            skLineSegment(sketch, "E6.1.1.2", {"start": v(-223.58, -61.5) * mm, "end": v(-186.92, 2) * mm});
            skLineSegment(sketch, "E6.1.1.3", {"start": v(-76.93, -61.5) * mm, "end": v(-113.6, -125) * mm});
            skLineSegment(sketch, "E6.1.1.4", {"start": v(-113.6, -125) * mm, "end": v(-186.92, -125) * mm});
            skLineSegment(sketch, "E6.1.1.5", {"start": v(-186.92, 2) * mm, "end": v(-113.6, 2) * mm});
            skLineSegment(sketch, "E6.1.2.0", {"start": v(-186.92, 27.4) * mm, "end": v(-223.58, 90.9) * mm});
            skLineSegment(sketch, "E6.1.2.1", {"start": v(-113.6, 154.4) * mm, "end": v(-76.93, 90.9) * mm});
            skLineSegment(sketch, "E6.1.2.2", {"start": v(-223.58, 90.9) * mm, "end": v(-186.92, 154.4) * mm});
            skLineSegment(sketch, "E6.1.2.3", {"start": v(-76.93, 90.9) * mm, "end": v(-113.6, 27.4) * mm});
            skLineSegment(sketch, "E6.1.2.4", {"start": v(-113.6, 27.4) * mm, "end": v(-186.92, 27.4) * mm});
            skLineSegment(sketch, "E6.1.2.5", {"start": v(-186.92, 154.4) * mm, "end": v(-113.6, 154.4) * mm});
            skLineSegment(sketch, "E6.1.3.0", {"start": v(-186.92, 179.8) * mm, "end": v(-223.58, 243.3) * mm});
            skLineSegment(sketch, "E6.1.3.1", {"start": v(-113.6, 306.8) * mm, "end": v(-76.93, 243.3) * mm});
            skLineSegment(sketch, "E6.1.3.2", {"start": v(-223.58, 243.3) * mm, "end": v(-186.92, 306.8) * mm});
            skLineSegment(sketch, "E6.1.3.3", {"start": v(-76.93, 243.3) * mm, "end": v(-113.6, 179.8) * mm});
            skLineSegment(sketch, "E6.1.3.4", {"start": v(-113.6, 179.8) * mm, "end": v(-186.92, 179.8) * mm});
            skLineSegment(sketch, "E6.1.3.5", {"start": v(-186.92, 306.8) * mm, "end": v(-113.6, 306.8) * mm});
            skLineSegment(sketch, "E6.2.0.0", {"start": v(67.08, -277.4) * mm, "end": v(30.42, -213.9) * mm});
            skLineSegment(sketch, "E6.2.0.1", {"start": v(140.4, -150.4) * mm, "end": v(177.07, -213.9) * mm});
            skLineSegment(sketch, "E6.2.0.2", {"start": v(30.42, -213.9) * mm, "end": v(67.08, -150.4) * mm});
            skLineSegment(sketch, "E6.2.0.3", {"start": v(177.07, -213.9) * mm, "end": v(140.4, -277.4) * mm});
            skLineSegment(sketch, "E6.2.0.4", {"start": v(140.4, -277.4) * mm, "end": v(67.08, -277.4) * mm});
            skLineSegment(sketch, "E6.2.0.5", {"start": v(67.08, -150.4) * mm, "end": v(140.4, -150.4) * mm});
            skLineSegment(sketch, "E6.2.1.0", {"start": v(67.08, -125) * mm, "end": v(30.42, -61.5) * mm});
            skLineSegment(sketch, "E6.2.1.1", {"start": v(140.4, 2) * mm, "end": v(177.07, -61.5) * mm});
            skLineSegment(sketch, "E6.2.1.2", {"start": v(30.42, -61.5) * mm, "end": v(67.08, 2) * mm});
            skLineSegment(sketch, "E6.2.1.3", {"start": v(177.07, -61.5) * mm, "end": v(140.4, -125) * mm});
            skLineSegment(sketch, "E6.2.1.4", {"start": v(140.4, -125) * mm, "end": v(67.08, -125) * mm});
            skLineSegment(sketch, "E6.2.1.5", {"start": v(67.08, 2) * mm, "end": v(140.4, 2) * mm});
            skLineSegment(sketch, "E6.2.2.0", {"start": v(67.08, 27.4) * mm, "end": v(30.42, 90.9) * mm});
            skLineSegment(sketch, "E6.2.2.1", {"start": v(140.4, 154.4) * mm, "end": v(177.07, 90.9) * mm});
            skLineSegment(sketch, "E6.2.2.2", {"start": v(30.42, 90.9) * mm, "end": v(67.08, 154.4) * mm});
            skLineSegment(sketch, "E6.2.2.3", {"start": v(177.07, 90.9) * mm, "end": v(140.4, 27.4) * mm});
            skLineSegment(sketch, "E6.2.2.4", {"start": v(140.4, 27.4) * mm, "end": v(67.08, 27.4) * mm});
            skLineSegment(sketch, "E6.2.2.5", {"start": v(67.08, 154.4) * mm, "end": v(140.4, 154.4) * mm});
            skLineSegment(sketch, "E6.2.3.0", {"start": v(67.08, 179.8) * mm, "end": v(30.42, 243.3) * mm});
            skLineSegment(sketch, "E6.2.3.1", {"start": v(140.4, 306.8) * mm, "end": v(177.07, 243.3) * mm});
            skLineSegment(sketch, "E6.2.3.2", {"start": v(30.42, 243.3) * mm, "end": v(67.08, 306.8) * mm});
            skLineSegment(sketch, "E6.2.3.3", {"start": v(177.07, 243.3) * mm, "end": v(140.4, 179.8) * mm});
            skLineSegment(sketch, "E6.2.3.4", {"start": v(140.4, 179.8) * mm, "end": v(67.08, 179.8) * mm});
            skLineSegment(sketch, "E6.2.3.5", {"start": v(67.08, 306.8) * mm, "end": v(140.4, 306.8) * mm});
            skLineSegment(sketch, "E6.3.0.0", {"start": v(321.08, -277.4) * mm, "end": v(284.42, -213.9) * mm});
            skLineSegment(sketch, "E6.3.0.1", {"start": v(394.4, -150.4) * mm, "end": v(431.07, -213.9) * mm});
            skLineSegment(sketch, "E6.3.0.2", {"start": v(284.42, -213.9) * mm, "end": v(321.08, -150.4) * mm});
            skLineSegment(sketch, "E6.3.0.3", {"start": v(431.07, -213.9) * mm, "end": v(394.4, -277.4) * mm});
            skLineSegment(sketch, "E6.3.0.4", {"start": v(394.4, -277.4) * mm, "end": v(321.08, -277.4) * mm});
            skLineSegment(sketch, "E6.3.0.5", {"start": v(321.08, -150.4) * mm, "end": v(394.4, -150.4) * mm});
            skLineSegment(sketch, "E6.3.1.0", {"start": v(321.08, -125) * mm, "end": v(284.42, -61.5) * mm});
            skLineSegment(sketch, "E6.3.1.1", {"start": v(394.4, 2) * mm, "end": v(431.07, -61.5) * mm});
            skLineSegment(sketch, "E6.3.1.2", {"start": v(284.42, -61.5) * mm, "end": v(321.08, 2) * mm});
            skLineSegment(sketch, "E6.3.1.3", {"start": v(431.07, -61.5) * mm, "end": v(394.4, -125) * mm});
            skLineSegment(sketch, "E6.3.1.4", {"start": v(394.4, -125) * mm, "end": v(321.08, -125) * mm});
            skLineSegment(sketch, "E6.3.1.5", {"start": v(321.08, 2) * mm, "end": v(394.4, 2) * mm});
            skLineSegment(sketch, "E6.3.2.0", {"start": v(321.08, 27.4) * mm, "end": v(284.42, 90.9) * mm});
            skLineSegment(sketch, "E6.3.2.1", {"start": v(394.4, 154.4) * mm, "end": v(431.07, 90.9) * mm});
            skLineSegment(sketch, "E6.3.2.2", {"start": v(284.42, 90.9) * mm, "end": v(321.08, 154.4) * mm});
            skLineSegment(sketch, "E6.3.2.3", {"start": v(431.07, 90.9) * mm, "end": v(394.4, 27.4) * mm});
            skLineSegment(sketch, "E6.3.2.4", {"start": v(394.4, 27.4) * mm, "end": v(321.08, 27.4) * mm});
            skLineSegment(sketch, "E6.3.2.5", {"start": v(321.08, 154.4) * mm, "end": v(394.4, 154.4) * mm});
            skLineSegment(sketch, "E6.3.3.0", {"start": v(321.08, 179.8) * mm, "end": v(284.42, 243.3) * mm});
            skLineSegment(sketch, "E6.3.3.1", {"start": v(394.4, 306.8) * mm, "end": v(431.07, 243.3) * mm});
            skLineSegment(sketch, "E6.3.3.2", {"start": v(284.42, 243.3) * mm, "end": v(321.08, 306.8) * mm});
            skLineSegment(sketch, "E6.3.3.3", {"start": v(431.07, 243.3) * mm, "end": v(394.4, 179.8) * mm});
            skLineSegment(sketch, "E6.3.3.4", {"start": v(394.4, 179.8) * mm, "end": v(321.08, 179.8) * mm});
            skLineSegment(sketch, "E6.3.3.5", {"start": v(321.08, 306.8) * mm, "end": v(394.4, 306.8) * mm});
            skLineSegment(sketch, "E6.4.0.0", {"start": v(575.08, -277.4) * mm, "end": v(538.42, -213.9) * mm});
            skLineSegment(sketch, "E6.4.0.1", {"start": v(648.4, -150.4) * mm, "end": v(685.07, -213.9) * mm});
            skLineSegment(sketch, "E6.4.0.2", {"start": v(538.42, -213.9) * mm, "end": v(575.08, -150.4) * mm});
            skLineSegment(sketch, "E6.4.0.3", {"start": v(685.07, -213.9) * mm, "end": v(648.4, -277.4) * mm});
            skLineSegment(sketch, "E6.4.0.4", {"start": v(648.4, -277.4) * mm, "end": v(575.08, -277.4) * mm});
            skLineSegment(sketch, "E6.4.0.5", {"start": v(575.08, -150.4) * mm, "end": v(648.4, -150.4) * mm});
            skLineSegment(sketch, "E6.4.1.0", {"start": v(575.08, -125) * mm, "end": v(538.42, -61.5) * mm});
            skLineSegment(sketch, "E6.4.1.1", {"start": v(648.4, 2) * mm, "end": v(685.07, -61.5) * mm});
            skLineSegment(sketch, "E6.4.1.2", {"start": v(538.42, -61.5) * mm, "end": v(575.08, 2) * mm});
            skLineSegment(sketch, "E6.4.1.3", {"start": v(685.07, -61.5) * mm, "end": v(648.4, -125) * mm});
            skLineSegment(sketch, "E6.4.1.4", {"start": v(648.4, -125) * mm, "end": v(575.08, -125) * mm});
            skLineSegment(sketch, "E6.4.1.5", {"start": v(575.08, 2) * mm, "end": v(648.4, 2) * mm});
            skLineSegment(sketch, "E6.4.2.0", {"start": v(575.08, 27.4) * mm, "end": v(538.42, 90.9) * mm});
            skLineSegment(sketch, "E6.4.2.1", {"start": v(648.4, 154.4) * mm, "end": v(685.07, 90.9) * mm});
            skLineSegment(sketch, "E6.4.2.2", {"start": v(538.42, 90.9) * mm, "end": v(575.08, 154.4) * mm});
            skLineSegment(sketch, "E6.4.2.3", {"start": v(685.07, 90.9) * mm, "end": v(648.4, 27.4) * mm});
            skLineSegment(sketch, "E6.4.2.4", {"start": v(648.4, 27.4) * mm, "end": v(575.08, 27.4) * mm});
            skLineSegment(sketch, "E6.4.2.5", {"start": v(575.08, 154.4) * mm, "end": v(648.4, 154.4) * mm});
            skLineSegment(sketch, "E6.4.3.0", {"start": v(575.08, 179.8) * mm, "end": v(538.42, 243.3) * mm});
            skLineSegment(sketch, "E6.4.3.1", {"start": v(648.4, 306.8) * mm, "end": v(685.07, 243.3) * mm});
            skLineSegment(sketch, "E6.4.3.2", {"start": v(538.42, 243.3) * mm, "end": v(575.08, 306.8) * mm});
            skLineSegment(sketch, "E6.4.3.3", {"start": v(685.07, 243.3) * mm, "end": v(648.4, 179.8) * mm});
            skLineSegment(sketch, "E6.4.3.4", {"start": v(648.4, 179.8) * mm, "end": v(575.08, 179.8) * mm});
            skLineSegment(sketch, "E6.4.3.5", {"start": v(575.08, 306.8) * mm, "end": v(648.4, 306.8) * mm});
            skLineSegment(sketch, "E6.5.0.0", {"start": v(829.08, -277.4) * mm, "end": v(792.42, -213.9) * mm});
            skLineSegment(sketch, "E6.5.0.1", {"start": v(902.4, -150.4) * mm, "end": v(939.07, -213.9) * mm});
            skLineSegment(sketch, "E6.5.0.2", {"start": v(792.42, -213.9) * mm, "end": v(829.08, -150.4) * mm});
            skLineSegment(sketch, "E6.5.0.3", {"start": v(939.07, -213.9) * mm, "end": v(902.4, -277.4) * mm});
            skLineSegment(sketch, "E6.5.0.4", {"start": v(902.4, -277.4) * mm, "end": v(829.08, -277.4) * mm});
            skLineSegment(sketch, "E6.5.0.5", {"start": v(829.08, -150.4) * mm, "end": v(902.4, -150.4) * mm});
            skLineSegment(sketch, "E6.5.1.0", {"start": v(829.08, -125) * mm, "end": v(792.42, -61.5) * mm});
            skLineSegment(sketch, "E6.5.1.1", {"start": v(902.4, 2) * mm, "end": v(939.07, -61.5) * mm});
            skLineSegment(sketch, "E6.5.1.2", {"start": v(792.42, -61.5) * mm, "end": v(829.08, 2) * mm});
            skLineSegment(sketch, "E6.5.1.3", {"start": v(939.07, -61.5) * mm, "end": v(902.4, -125) * mm});
            skLineSegment(sketch, "E6.5.1.4", {"start": v(902.4, -125) * mm, "end": v(829.08, -125) * mm});
            skLineSegment(sketch, "E6.5.1.5", {"start": v(829.08, 2) * mm, "end": v(902.4, 2) * mm});
            skLineSegment(sketch, "E6.5.2.0", {"start": v(829.08, 27.4) * mm, "end": v(792.42, 90.9) * mm});
            skLineSegment(sketch, "E6.5.2.1", {"start": v(902.4, 154.4) * mm, "end": v(939.07, 90.9) * mm});
            skLineSegment(sketch, "E6.5.2.2", {"start": v(792.42, 90.9) * mm, "end": v(829.08, 154.4) * mm});
            skLineSegment(sketch, "E6.5.2.3", {"start": v(939.07, 90.9) * mm, "end": v(902.4, 27.4) * mm});
            skLineSegment(sketch, "E6.5.2.4", {"start": v(902.4, 27.4) * mm, "end": v(829.08, 27.4) * mm});
            skLineSegment(sketch, "E6.5.2.5", {"start": v(829.08, 154.4) * mm, "end": v(902.4, 154.4) * mm});
            skLineSegment(sketch, "E6.5.3.0", {"start": v(829.08, 179.8) * mm, "end": v(792.42, 243.3) * mm});
            skLineSegment(sketch, "E6.5.3.1", {"start": v(902.4, 306.8) * mm, "end": v(939.07, 243.3) * mm});
            skLineSegment(sketch, "E6.5.3.2", {"start": v(792.42, 243.3) * mm, "end": v(829.08, 306.8) * mm});
            skLineSegment(sketch, "E6.5.3.3", {"start": v(939.07, 243.3) * mm, "end": v(902.4, 179.8) * mm});
            skLineSegment(sketch, "E6.5.3.4", {"start": v(902.4, 179.8) * mm, "end": v(829.08, 179.8) * mm});
            skLineSegment(sketch, "E6.5.3.5", {"start": v(829.08, 306.8) * mm, "end": v(902.4, 306.8) * mm});
            skLineSegment(sketch, "E6.direction1", {"start": v(-477.58, -213.9) * mm, "end": v(-223.58, -213.9) * mm, "construction": true});
            skLineSegment(sketch, "E6.direction2", {"start": v(-477.58, -213.9) * mm, "end": v(-477.58, -61.5) * mm, "construction": true});
            skSolve(sketch);
        }
        {
            var Q0;
            {var subQ54=sQuery(id+"F0.wireOp",EDGE,"E1.1");Q0=makeQuery(id+"F0.imprint","IMPRINT",FACE,{"disambiguationData":[TD([[makeQuery(id+"F0.imprint","IMPRINT",EDGE,{"derivedFrom":subQ54}),1.0]])]});}
            extrude(context, id + "F1", {"entities" : qUnion([Q0]), "depth" : 3.17 * mm});
        }
        {
            var Q0;
            {var subQ0=sQuery(id+"F0.wireOp",EDGE,"E0.left");Q0=makeQuery(id+"F1.opExtrude","CAP_EDGE",EDGE,{"disambiguationData":[OSD([subQ0]),TDD([makeQuery(id+"F0.imprint","IMPRINT",EDGE,{"disambiguationData":[TD([[makeQuery(id+"F0.imprint","INTERSECT",VERTEX,{"derivedFrom":[subQ0,sQuery(id+"F0.wireOp",EDGE,"E5.0.4.1")]}),-1.0]])],"derivedFrom":subQ0})])],"isStart":true});}
            chamfer(context, id + "F2", {"entities" : qUnion([Q0]), "chamferType" : ChamferType.OFFSET_ANGLE, "width" : 3.17 * mm, "oppositeDirection" : false, "angle" : 30 * degree, "tangentPropagation" : true});
        }
        {
            var Q0;
            {var subQ0=sQuery(id+"F0.wireOp",EDGE,"E0.left");Q0=makeQuery(id+"F1.opExtrude","CAP_EDGE",EDGE,{"disambiguationData":[OSD([subQ0]),TDD([makeQuery(id+"F0.imprint","IMPRINT",EDGE,{"disambiguationData":[TD([[makeQuery(id+"F0.imprint","INTERSECT",VERTEX,{"derivedFrom":[subQ0,sQuery(id+"F0.wireOp",EDGE,"E5.0.3.1")]}),-1.0]])],"derivedFrom":subQ0})])],"isStart":true});}
            chamfer(context, id + "F3", {"entities" : qUnion([Q0]), "chamferType" : ChamferType.OFFSET_ANGLE, "width" : 3.17 * mm, "oppositeDirection" : false, "angle" : 30 * degree});
        }
        {
            var Q0;
            {var subQ0=sQuery(id+"F0.wireOp",EDGE,"E0.left");Q0=makeQuery(id+"F1.opExtrude","CAP_EDGE",EDGE,{"disambiguationData":[OSD([subQ0]),TDD([makeQuery(id+"F0.imprint","IMPRINT",EDGE,{"disambiguationData":[TD([[makeQuery(id+"F0.imprint","INTERSECT",VERTEX,{"derivedFrom":[subQ0,sQuery(id+"F0.wireOp",EDGE,"E5.0.2.1")]}),-1.0]])],"derivedFrom":subQ0})])],"isStart":true});}
            chamfer(context, id + "F4", {"entities" : qUnion([Q0]), "chamferType" : ChamferType.OFFSET_ANGLE, "width" : 3.17 * mm, "oppositeDirection" : false, "angle" : 30 * degree, "tangentPropagation" : true});
        }
        {
            var Q0;
            {var subQ0=sQuery(id+"F0.wireOp",EDGE,"E0.left");Q0=makeQuery(id+"F1.opExtrude","CAP_EDGE",EDGE,{"disambiguationData":[OSD([subQ0]),TDD([makeQuery(id+"F0.imprint","IMPRINT",EDGE,{"disambiguationData":[TD([[makeQuery(id+"F0.imprint","INTERSECT",VERTEX,{"derivedFrom":[subQ0,sQuery(id+"F0.wireOp",EDGE,"E5.0.1.1")]}),-1.0]])],"derivedFrom":subQ0})])],"isStart":true});}
            chamfer(context, id + "F5", {"entities" : qUnion([Q0]), "chamferType" : ChamferType.OFFSET_ANGLE, "width" : 3.17 * mm, "oppositeDirection" : false, "angle" : 30 * degree, "tangentPropagation" : true});
        }
        {
            var Q0;
            {var subQ0=sQuery(id+"F0.wireOp",EDGE,"E0.right");Q0=makeQuery(id+"F1.opExtrude","CAP_EDGE",EDGE,{"disambiguationData":[OSD([subQ0]),TDD([makeQuery(id+"F0.imprint","IMPRINT",EDGE,{"disambiguationData":[TD([[makeQuery(id+"F0.imprint","INTERSECT",VERTEX,{"derivedFrom":[subQ0,sQuery(id+"F0.wireOp",EDGE,"E5.6.4.1")]}),-1.0]])],"derivedFrom":subQ0})])],"isStart":true});}
            chamfer(context, id + "F6", {"entities" : qUnion([Q0]), "chamferType" : ChamferType.OFFSET_ANGLE, "width" : 1.84 * mm, "oppositeDirection" : false, "angle" : 60 * degree, "tangentPropagation" : true});
        }
        {
            var Q0;
            {var subQ0=sQuery(id+"F0.wireOp",EDGE,"E0.right");Q0=makeQuery(id+"F1.opExtrude","CAP_EDGE",EDGE,{"disambiguationData":[OSD([subQ0]),TDD([makeQuery(id+"F0.imprint","IMPRINT",EDGE,{"disambiguationData":[TD([[makeQuery(id+"F0.imprint","INTERSECT",VERTEX,{"derivedFrom":[subQ0,sQuery(id+"F0.wireOp",EDGE,"E5.6.3.1")]}),-1.0]])],"derivedFrom":subQ0})])],"isStart":true});}
            chamfer(context, id + "F7", {"entities" : qUnion([Q0]), "chamferType" : ChamferType.OFFSET_ANGLE, "width" : 1.84 * mm, "oppositeDirection" : false, "angle" : 60 * degree, "tangentPropagation" : true});
        }
        {
            var Q0;
            {var subQ0=sQuery(id+"F0.wireOp",EDGE,"E0.right");Q0=makeQuery(id+"F1.opExtrude","CAP_EDGE",EDGE,{"disambiguationData":[OSD([subQ0]),TDD([makeQuery(id+"F0.imprint","IMPRINT",EDGE,{"disambiguationData":[TD([[makeQuery(id+"F0.imprint","INTERSECT",VERTEX,{"derivedFrom":[subQ0,sQuery(id+"F0.wireOp",EDGE,"E5.6.2.1")]}),-1.0]])],"derivedFrom":subQ0})])],"isStart":true});}
            chamfer(context, id + "F8", {"entities" : qUnion([Q0]), "chamferType" : ChamferType.OFFSET_ANGLE, "width" : 1.84 * mm, "oppositeDirection" : false, "angle" : 60 * degree, "tangentPropagation" : true});
        }
        {
            var Q0;
            {var subQ0=sQuery(id+"F0.wireOp",EDGE,"E0.right");Q0=makeQuery(id+"F1.opExtrude","CAP_EDGE",EDGE,{"disambiguationData":[OSD([subQ0]),TDD([makeQuery(id+"F0.imprint","IMPRINT",EDGE,{"disambiguationData":[TD([[makeQuery(id+"F0.imprint","INTERSECT",VERTEX,{"derivedFrom":[subQ0,sQuery(id+"F0.wireOp",EDGE,"E5.6.1.1")]}),-1.0]])],"derivedFrom":subQ0})])],"isStart":true});}
            chamfer(context, id + "F9", {"entities" : qUnion([Q0]), "chamferType" : ChamferType.OFFSET_ANGLE, "width" : 1.84 * mm, "oppositeDirection" : false, "angle" : 60 * degree, "tangentPropagation" : true});
        }
    });
